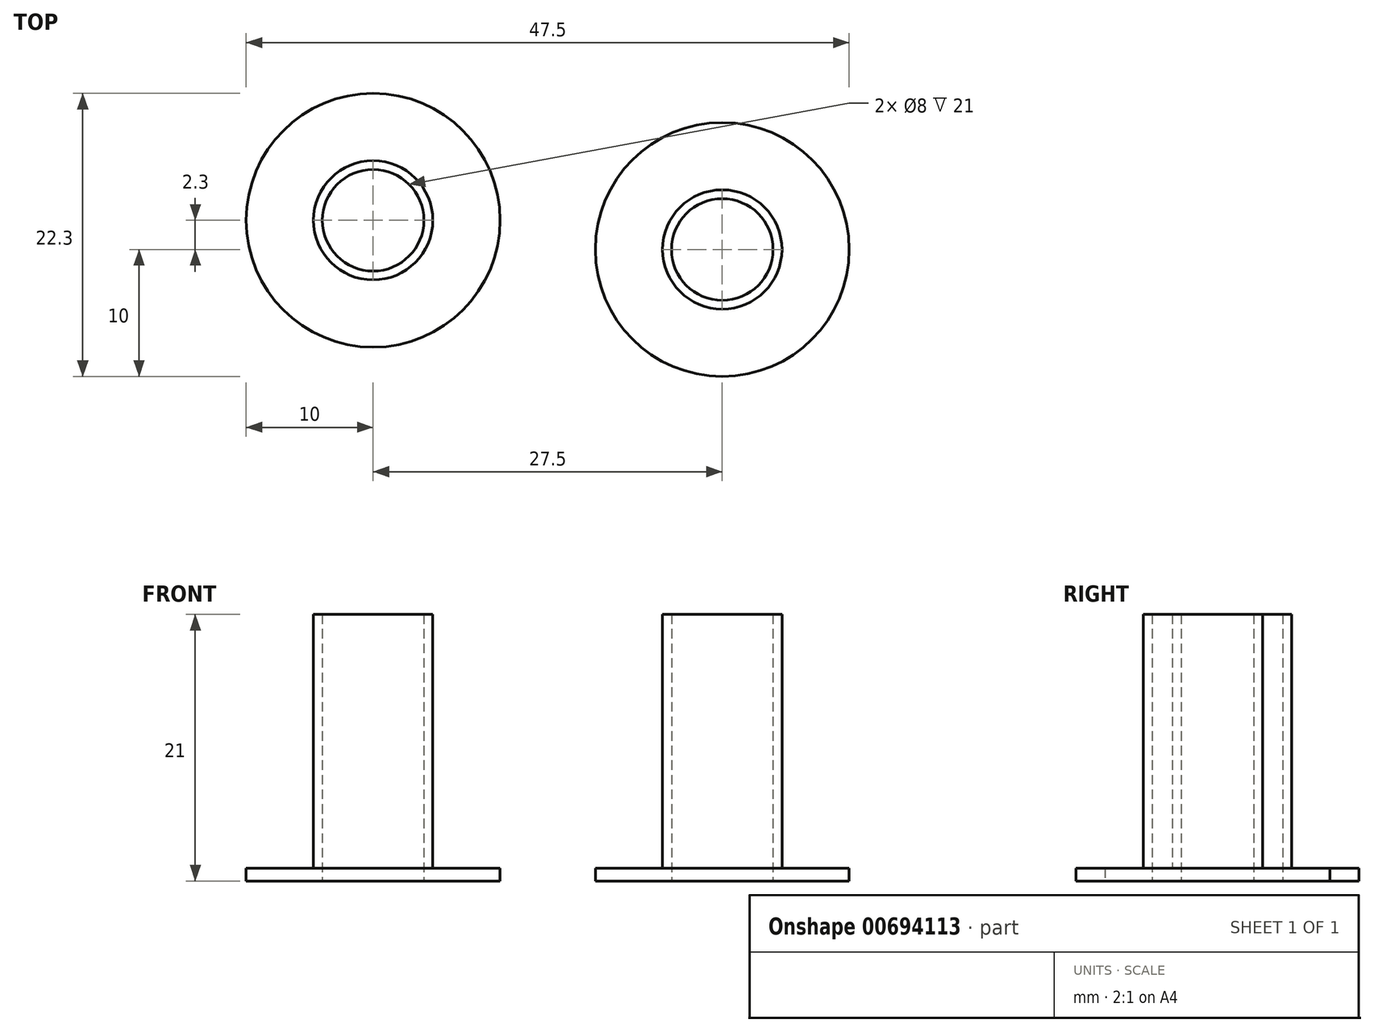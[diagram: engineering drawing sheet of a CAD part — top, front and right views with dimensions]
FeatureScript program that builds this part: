
annotation { "Feature Type Name" : "Feature", "Feature Type Description" : "" }
export const myFeature = defineFeature(function(context is Context, id is Id, definition is map)
    precondition{}
    {
        {
            var Q0;
            Q0=qCreatedBy(makeId("Front.planeOp"),FACE);
            var sketch = newSketch(context, id + "F0", { "sketchPlane" : qUnion([Q0])});
            skLineSegment(sketch, "E0", {"start": v(0, 0) * mm, "end": v(4, 0) * mm, "construction": true});
            skLineSegment(sketch, "E1", {"start": v(4, 0) * mm, "end": v(4.7, 0) * mm});
            skPoint(sketch, "E1.endSnap0", {"position": v(2, 0) * mm});
            skLineSegment(sketch, "E2.top", {"start": v(4, 20) * mm, "end": v(4.7, 20) * mm});
            skLineSegment(sketch, "E2.left", {"start": v(4, 0) * mm, "end": v(4, 20) * mm});
            skLineSegment(sketch, "E2.right", {"start": v(4.7, 0) * mm, "end": v(4.7, 20) * mm});
            skLineSegment(sketch, "E3.bottom", {"start": v(4, 0) * mm, "end": v(10, 0) * mm});
            skLineSegment(sketch, "E3.top", {"start": v(4, -1) * mm, "end": v(10, -1) * mm});
            skLineSegment(sketch, "E3.left", {"start": v(4, 0) * mm, "end": v(4, -1) * mm});
            skLineSegment(sketch, "E3.right", {"start": v(10, 0) * mm, "end": v(10, -1) * mm});
            skLineSegment(sketch, "E4", {"start": v(0, 0) * mm, "end": v(0, 16.1) * mm, "construction": true});
            skSolve(sketch);
        }
        {
            var Q0;
            Q0 = qSketchRegion(id + "F0", true);
            var Q1;
            Q1=sQuery(id+"F0.wireOp",EDGE,"E4");
            revolve(context, id + "F1", {"entities" : qUnion([Q0]), "axis" : qUnion([Q1]), "revolveType" : RevolveType.FULL});
        }
        {
            var Q0;
            Q0=makeQuery(id+"F1.opRevolve","SWEPT_BODY",BODY,{"disambiguationData":[OSD([sQuery(id+"F0.wireOp",EDGE,"E2.top"),sQuery(id+"F0.wireOp",EDGE,"E2.left"),sQuery(id+"F0.wireOp",EDGE,"E2.right"),sQuery(id+"F0.wireOp",EDGE,"E3.bottom"),sQuery(id+"F0.wireOp",EDGE,"E3.top"),sQuery(id+"F0.wireOp",EDGE,"E3.left"),sQuery(id+"F0.wireOp",EDGE,"E3.right")])]});
            transform(context, id + "F2", {"entities" : qUnion([Q0]), "transformType" : TransformType.TRANSLATION_3D, "dx" : 27.5 * mm, "dy" : -2.3 * mm, "dz" : 0 * mm, "makeCopy" : true});
        }
        {
            var Q0;
            Q0=makeQuery(id+"F1.opRevolve","SWEPT_BODY",BODY,{"disambiguationData":[OSD([sQuery(id+"F0.wireOp",EDGE,"E2.top"),sQuery(id+"F0.wireOp",EDGE,"E2.left"),sQuery(id+"F0.wireOp",EDGE,"E2.right"),sQuery(id+"F0.wireOp",EDGE,"E3.bottom"),sQuery(id+"F0.wireOp",EDGE,"E3.top"),sQuery(id+"F0.wireOp",EDGE,"E3.left"),sQuery(id+"F0.wireOp",EDGE,"E3.right")])]});
            transform(context, id + "F3", {"entities" : qUnion([Q0]), "transformType" : TransformType.COPY});
        }
        {
            var Q0;
            Q0=makeQuery(id+"F3.opPattern","COPY",BODY,{"derivedFrom":makeQuery(id+"F1.opRevolve","SWEPT_BODY",BODY,{"disambiguationData":[OSD([sQuery(id+"F0.wireOp",EDGE,"E2.top"),sQuery(id+"F0.wireOp",EDGE,"E2.left"),sQuery(id+"F0.wireOp",EDGE,"E2.right"),sQuery(id+"F0.wireOp",EDGE,"E3.bottom"),sQuery(id+"F0.wireOp",EDGE,"E3.top"),sQuery(id+"F0.wireOp",EDGE,"E3.left"),sQuery(id+"F0.wireOp",EDGE,"E3.right")])]}),"instanceName":"1"});
            deleteBodies(context, id + "F4", {"entities" : qUnion([Q0])});
        }
    });
